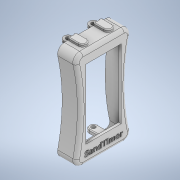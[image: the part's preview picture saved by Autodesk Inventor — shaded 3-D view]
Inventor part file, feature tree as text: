
AUTODESK INVENTOR PART (.ipt)
format: ipt  version: 2021 (Build 250183000, 183)  size: 602,624 bytes
history: native  units: mm
features: extrude x7, sketch x7, fillet x6, mirror x4, plane x3, shell x1, projected_geometry x1
ambient origin geometry x8: Origin, YZ Plane, XZ Plane, XY Plane, X Axis, Y Axis, Z Axis, Center Point
bodies: Solid1 (feature_tree)
feature tree (29):
  extrude  "Extrusion1"  Depth=11.0mm
  extrude  "Extrusion5"  Depth=2.0mm
  fillet  "Fillet1"  Radius=1.5mm
  shell  "Shell1"  Thickness=3.8mm
  extrude  "Extrusion9"  Depth=4.0mm
  plane  "Work Plane1"
  extrude  "Extrusion10"  Depth=41.0mm
  extrude  "Extrusion11"  TaperAngle=0.0deg  [1 undecoded]
  fillet  "Fillet4"  [1 undecoded]
  mirror  "Mirror1"
  plane  "Work Plane2"
  mirror  "Mirror2"
  extrude  "Extrusion12"  Depth=2.0mm
  extrude  "Extrusion13"  Depth=0.5mm TaperAngle=0.0deg
  fillet  "Fillet6"  Radius=2.4mm
  fillet  "Fillet7"  [1 undecoded]
  mirror  "Mirror3"
  plane  "Work Plane3"
  mirror  "Mirror4"
  fillet  "Fillet8"  Radius=0.5mm
  fillet  "Fillet9"  Radius=24.0mm
  sketch  "Sketch1"  dims[d0=11.0mm d1=27.0mm]
  sketch  "Sketch5"  dims[d2=58.0mm d3=0.0mm d4=2.0mm d5=1.5mm d26=3.8mm]
  sketch  "Sketch9"  dims[d27=0.0mm d28=0.0mm d29=4.0mm]
  sketch  "Sketch10"  dims[d53=21.0mm d54=41.0mm]
  sketch  "Sketch11"  dims[d55=6.54mm d56=0.0mm d57=0.0mm d58=-3.0mm]
  sketch  "Sketch12"  dims[d59=5.0mm d60=2.0mm]
  sketch  "Sketch13"  dims[d61=5.0mm d62=8.0mm d63=0.0mm d64=2.4mm d65=0.0mm d66=0.0mm d67=0.5mm d68=24.0mm d69=4.0mm d70=3.0mm d71=0.5mm d72=0.0mm d73=5.0mm d75=1.5mm d76=0.0mm d79=1.0mm d80=0.5mm d81=1.0mm d82=0.5mm]
  projected_geometry  "Project Cut Edges7"
note: 3 required parameter values undecoded (feature->parameter linkage not recoverable at this tier; creation-order binding heuristic only, values carry confidence <= 0.55)
